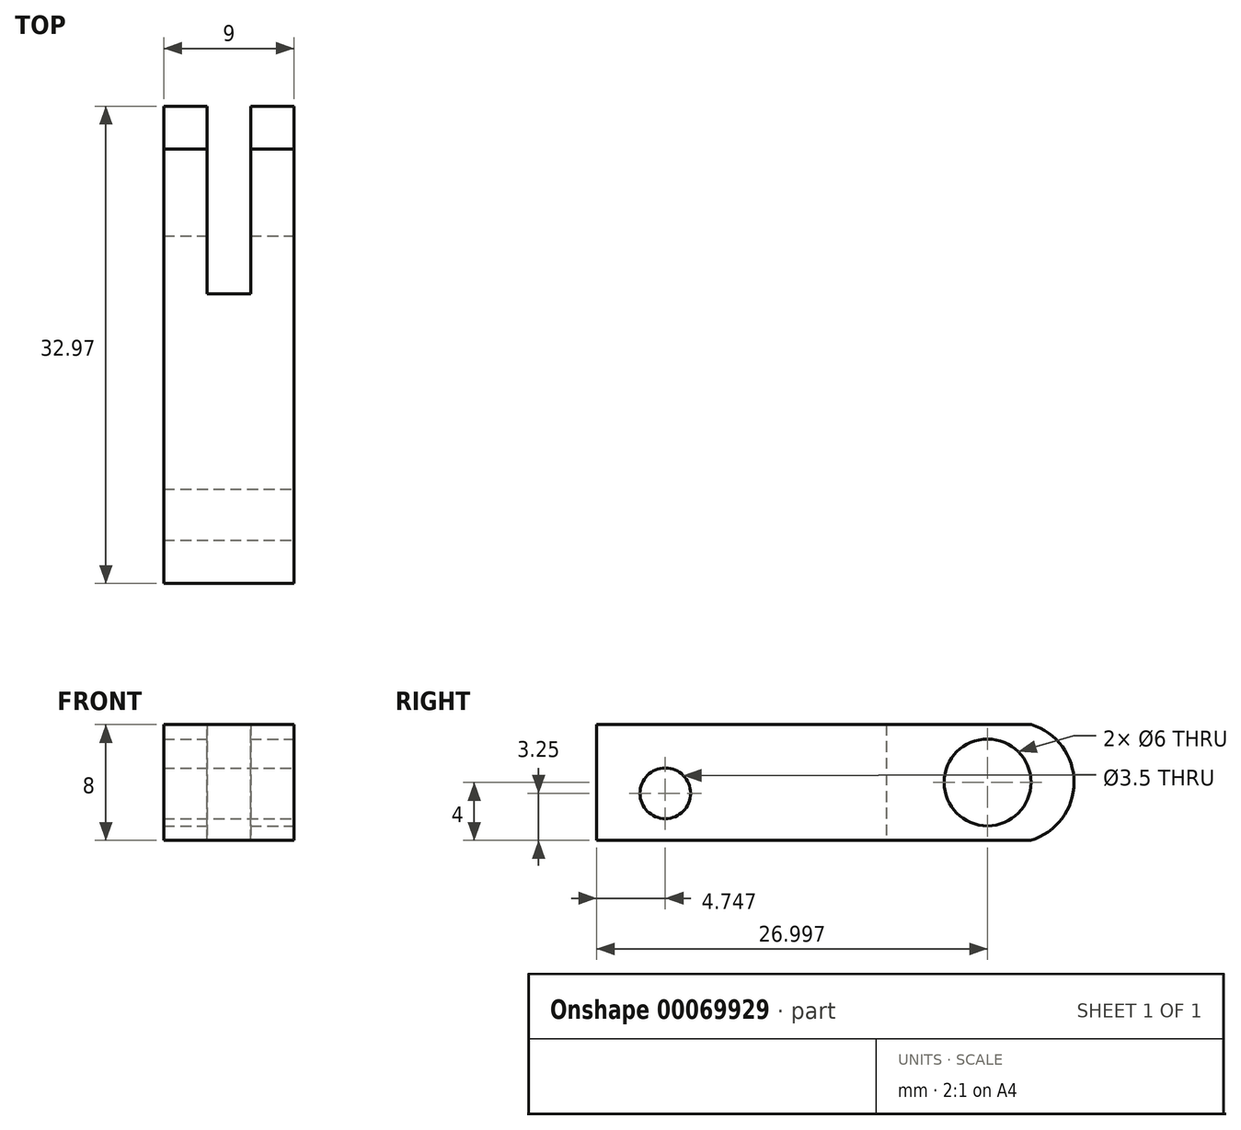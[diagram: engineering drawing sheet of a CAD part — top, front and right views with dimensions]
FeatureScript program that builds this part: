
annotation { "Feature Type Name" : "Feature", "Feature Type Description" : "" }
export const myFeature = defineFeature(function(context is Context, id is Id, definition is map)
    precondition{}
    {
        {
            var Q0;
            Q0=qCreatedBy(makeId("Top.planeOp"),FACE);
            var sketch = newSketch(context, id + "F0", { "sketchPlane" : qUnion([Q0])});
            skLineSegment(sketch, "E0.bottom", {"start": v(-37.51, 23.23) * mm, "end": v(-34.51, 23.23) * mm});
            skLineSegment(sketch, "E0.top", {"start": v(-37.51, 10.23) * mm, "end": v(-34.51, 10.23) * mm});
            skLineSegment(sketch, "E0.left", {"start": v(-37.51, 23.23) * mm, "end": v(-37.51, 10.23) * mm});
            skLineSegment(sketch, "E0.right", {"start": v(-34.51, 23.23) * mm, "end": v(-34.51, 10.23) * mm});
            skLineSegment(sketch, "E1.top", {"start": v(-31.51, 10.23) * mm, "end": v(-28.51, 10.23) * mm});
            skLineSegment(sketch, "E1.left", {"start": v(-31.51, 23.23) * mm, "end": v(-31.51, 10.23) * mm});
            skLineSegment(sketch, "E1.right", {"start": v(-28.51, 23.23) * mm, "end": v(-28.51, 10.23) * mm});
            skLineSegment(sketch, "E1.bottom", {"start": v(-31.51, 23.23) * mm, "end": v(-28.51, 23.23) * mm});
            skLineSegment(sketch, "E2.bottom", {"start": v(-37.51, 10.23) * mm, "end": v(-28.51, 10.23) * mm});
            skLineSegment(sketch, "E2.top", {"start": v(-37.51, 5.23) * mm, "end": v(-28.51, 5.23) * mm});
            skLineSegment(sketch, "E2.left", {"start": v(-37.51, 10.23) * mm, "end": v(-37.51, 5.23) * mm});
            skLineSegment(sketch, "E2.right", {"start": v(-28.51, 10.23) * mm, "end": v(-28.51, 5.23) * mm});
            skSolve(sketch);
        }
        {
            var Q0;
            Q0=makeQuery(id+"F0.imprint","IMPRINT",FACE,{"disambiguationData":[TD([[makeQuery(id+"F0.imprint","IMPRINT",EDGE,{"derivedFrom":sQuery(id+"F0.wireOp",EDGE,"E0.bottom")}),-1.0]])]});
            var Q1;
            {var subQ0=sQuery(id+"F0.wireOp",EDGE,"E1.left");Q1=makeQuery(id+"F0.imprint","IMPRINT",FACE,{"disambiguationData":[TD([[makeQuery(id+"F0.imprint","IMPRINT",EDGE,{"derivedFrom":subQ0}),1.0]])]});}
            var Q2;
            Q2=makeQuery(id+"F0.imprint","IMPRINT",FACE,{"disambiguationData":[TD([[makeQuery(id+"F0.imprint","IMPRINT",EDGE,{"derivedFrom":sQuery(id+"F0.wireOp",EDGE,"E2.top")}),1.0]])]});
            extrude(context, id + "F1", {"entities" : qUnion([Q0, Q1, Q2]), "depth" : 8 * mm});
        }
        {
            var Q0;
            Q0=makeQuery(id+"F1.opExtrude","SWEPT_FACE",FACE,{"disambiguationData":[OSD([sQuery(id+"F0.wireOp",EDGE,"E1.right"),sQuery(id+"F0.wireOp",EDGE,"E2.right")])]});
            var sketch = newSketch(context, id + "F2", { "sketchPlane" : qUnion([Q0])});
            skCircle(sketch, "E3", {"center": v(17.23, 4) * mm, "radius": 3 * mm});
            skArc(sketch, "E4", {"start": v(20.2, 0) * mm, "mid": v(23.2, 3.99) * mm, "end": v(20.23, 8) * mm});
            skSolve(sketch);
        }
        {
            var Q0;
            Q0=makeQuery(id+"F2.imprint","IMPRINT",FACE,{"disambiguationData":[TD([[makeQuery(id+"F2.imprint","IMPRINT",EDGE,{"derivedFrom":sQuery(id+"F2.wireOp",EDGE,"E3")}),1.0]])]});
            extrude(context, id + "F3", {"entities" : qUnion([Q0]), "operationType" : NewBodyOperationType.REMOVE, "oppositeDirection" : true, "depth" : 10 * mm});
        }
        {
            var Q0;
            {var subQ0=sQuery(id+"F2.wireOp",EDGE,"E4");Q0=makeQuery(id+"F2.imprint","IMPRINT",FACE,{"disambiguationData":[TD([[makeQuery(id+"F2.imprint","IMPRINT",EDGE,{"derivedFrom":subQ0}),-1.0]])]});}
            extrude(context, id + "F4", {"entities" : qUnion([Q0]), "operationType" : NewBodyOperationType.REMOVE, "oppositeDirection" : true, "depth" : 25 * mm});
        }
        {
            var Q0;
            Q0=makeQuery(id+"F1.opExtrude","SWEPT_FACE",FACE,{"disambiguationData":[OSD([sQuery(id+"F0.wireOp",EDGE,"E2.top")])]});
            extrude(context, id + "F5", {"entities" : qUnion([Q0]), "operationType" : NewBodyOperationType.ADD, "depth" : 15 * mm});
        }
        {
            var Q0;
            {var subQ0=sQuery(id+"F0.wireOp",EDGE,"E2.right");Q0=makeQuery(id+"F5.boolean.opBoolean","MERGE",FACE,{"derivedFrom":[makeQuery(id+"F1.opExtrude","SWEPT_FACE",FACE,{"disambiguationData":[OSD([sQuery(id+"F0.wireOp",EDGE,"E1.right"),subQ0])]}),makeQuery(id+"F5.opExtrude","SWEPT_FACE",FACE,{"disambiguationData":[OSD([sQuery(id+"F0.wireOp",EDGE,"E2.top"),subQ0])]})]});}
            var sketch = newSketch(context, id + "F6", { "sketchPlane" : qUnion([Q0])});
            skCircle(sketch, "E5", {"center": v(-5.02, 3.25) * mm, "radius": 1.75 * mm});
            skSolve(sketch);
        }
        {
            var Q0;
            Q0=makeQuery(id+"F6.imprint","IMPRINT",FACE,{"disambiguationData":[TD([[makeQuery(id+"F6.imprint","IMPRINT",EDGE,{"derivedFrom":sQuery(id+"F6.wireOp",EDGE,"E5")}),1.0]])]});
            extrude(context, id + "F7", {"entities" : qUnion([Q0]), "operationType" : NewBodyOperationType.REMOVE, "oppositeDirection" : true, "depth" : 25 * mm});
        }
    });
